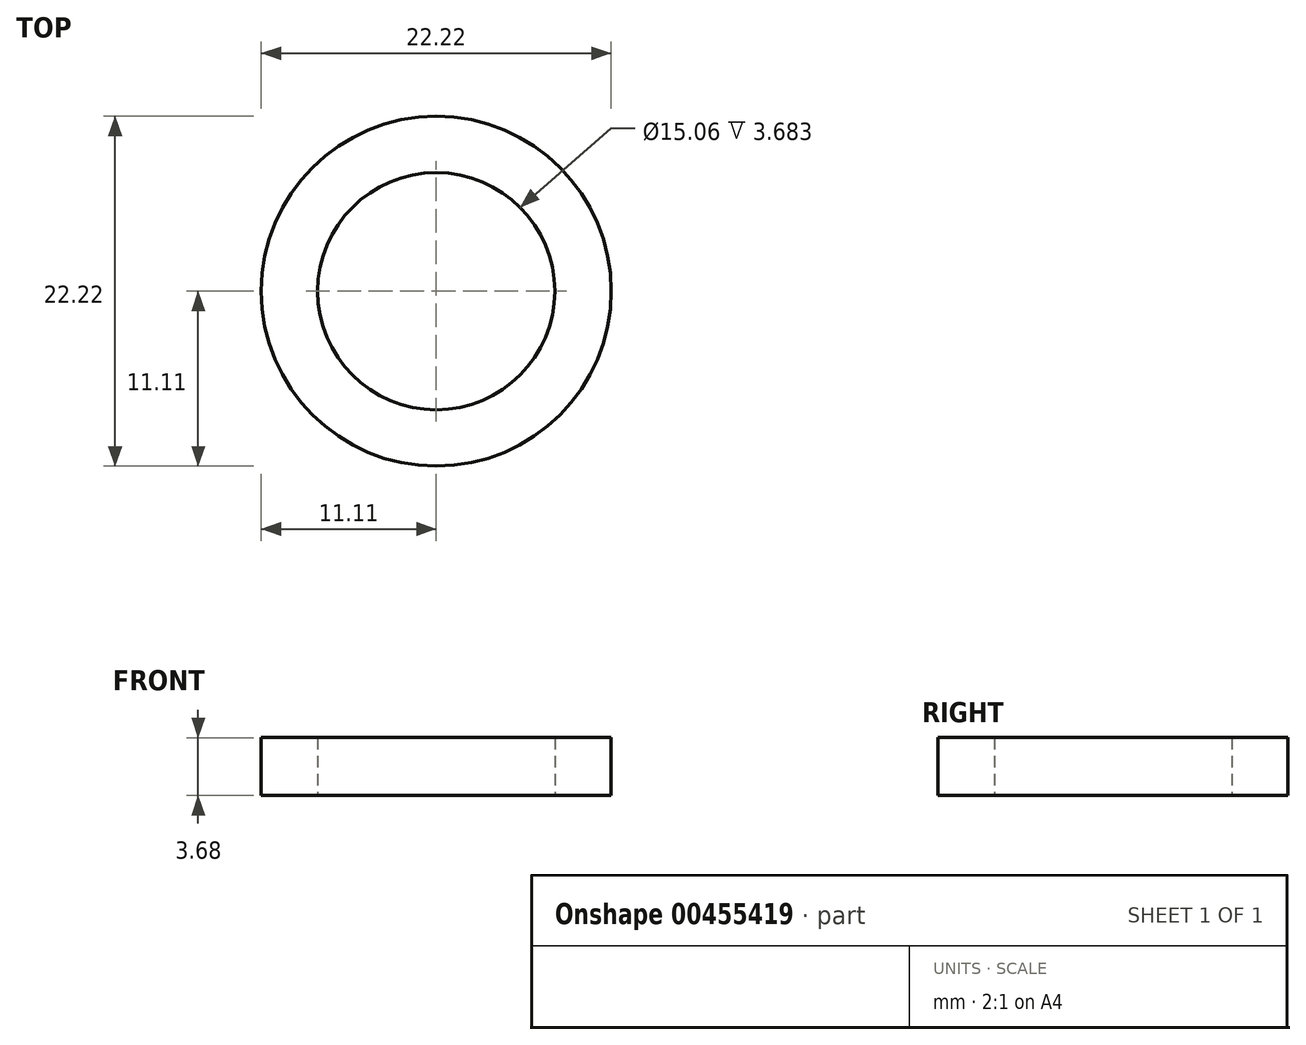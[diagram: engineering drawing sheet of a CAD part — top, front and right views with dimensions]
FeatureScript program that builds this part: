
annotation { "Feature Type Name" : "Feature", "Feature Type Description" : "" }
export const myFeature = defineFeature(function(context is Context, id is Id, definition is map)
    precondition{}
    {
        {
            var Q0;
            Q0=qCreatedBy(makeId("Top.planeOp"),FACE);
            var sketch = newSketch(context, id + "F0", { "sketchPlane" : qUnion([Q0])});
            skCircle(sketch, "E0", {"center": v(0, 0) * mm, "radius": 11.11 * mm});
            skCircle(sketch, "E1", {"center": v(0, 0) * mm, "radius": 7.53 * mm});
            skSolve(sketch);
        }
        {
            var Q0;
            Q0=makeQuery(id+"F0.imprint","IMPRINT",FACE,{"disambiguationData":[TD([[makeQuery(id+"F0.imprint","IMPRINT",EDGE,{"derivedFrom":sQuery(id+"F0.wireOp",EDGE,"E0")}),1.0]])]});
            extrude(context, id + "F1", {"entities" : qUnion([Q0]), "depth" : 3.68 * mm});
        }
    });
